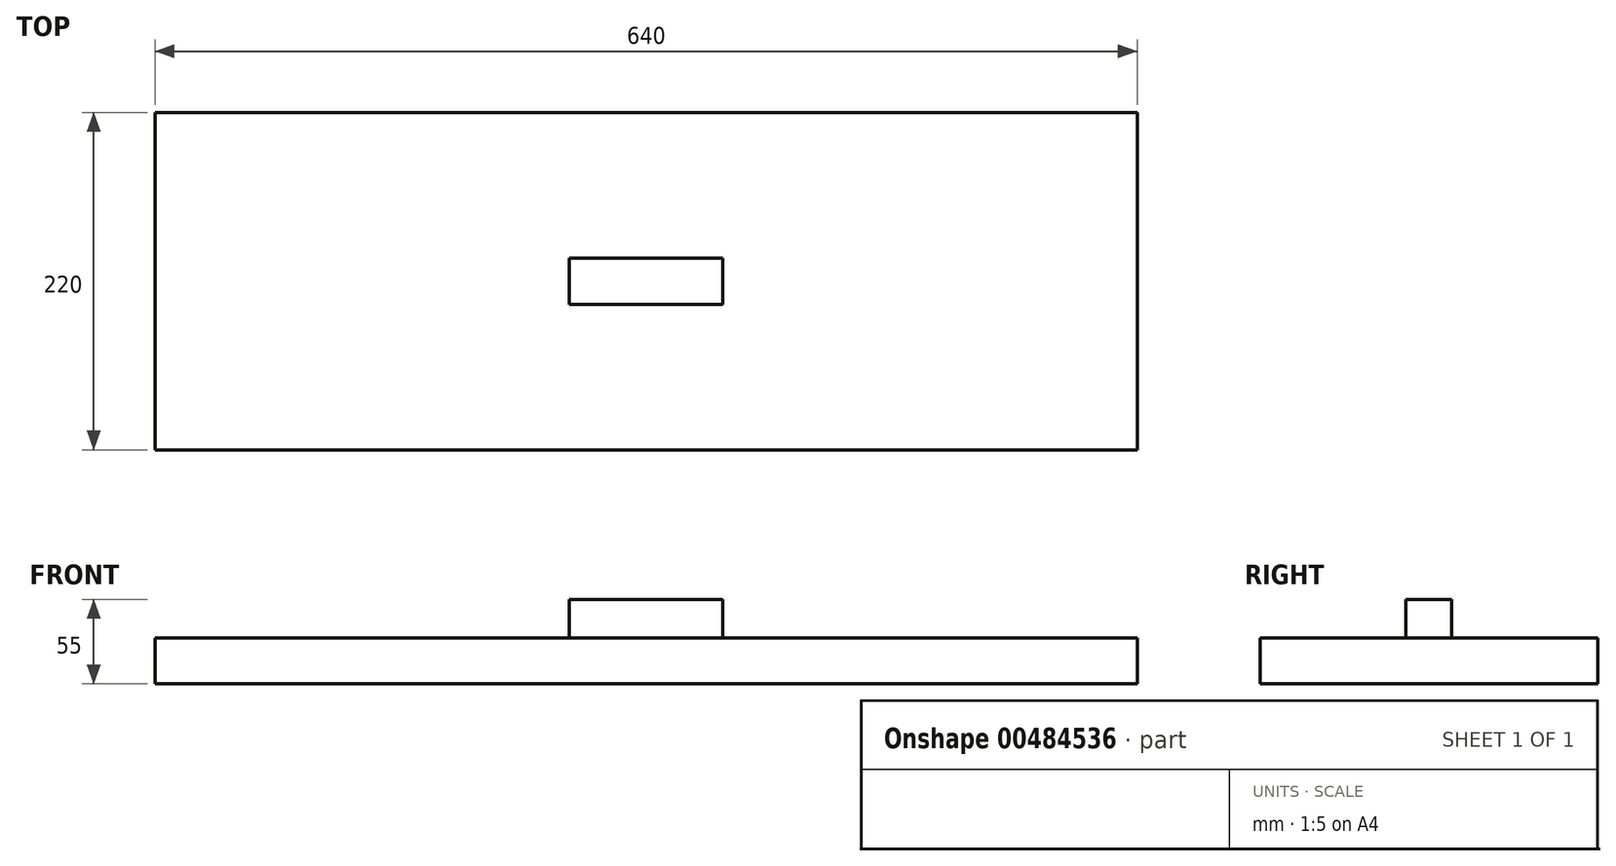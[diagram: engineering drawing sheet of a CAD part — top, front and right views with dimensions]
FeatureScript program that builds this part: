
annotation { "Feature Type Name" : "Feature", "Feature Type Description" : "" }
export const myFeature = defineFeature(function(context is Context, id is Id, definition is map)
    precondition{}
    {
        {
            var Q0;
            Q0=qCreatedBy(makeId("Top.planeOp"),FACE);
            var sketch = newSketch(context, id + "F0", { "sketchPlane" : qUnion([Q0])});
            skLineSegment(sketch, "E0.bottom", {"start": v(-509.87, -280.53) * mm, "end": v(130.13, -280.53) * mm});
            skLineSegment(sketch, "E0.top", {"start": v(-509.87, -60.53) * mm, "end": v(130.13, -60.53) * mm});
            skLineSegment(sketch, "E0.left", {"start": v(-509.87, -280.53) * mm, "end": v(-509.87, -60.53) * mm});
            skLineSegment(sketch, "E0.right", {"start": v(130.13, -280.53) * mm, "end": v(130.13, -60.53) * mm});
            skSolve(sketch);
        }
        {
            var Q0;
            Q0=qSketchRegion(id+"F0",true);
            extrude(context, id + "F1", {"entities" : qUnion([Q0]), "depth" : 30 * mm});
        }
        {
            var Q0;
            Q0=makeQuery(id+"F1.opExtrude","CAP_FACE",FACE,{"disambiguationData":[OSD([sQuery(id+"F0.wireOp",EDGE,"E0.bottom"),sQuery(id+"F0.wireOp",EDGE,"E0.top"),sQuery(id+"F0.wireOp",EDGE,"E0.left"),sQuery(id+"F0.wireOp",EDGE,"E0.right")])],"isStart":false});
            var sketch = newSketch(context, id + "F2", { "sketchPlane" : qUnion([Q0])});
            skLineSegment(sketch, "E1.bottom", {"start": v(-239.87, -185.53) * mm, "end": v(-139.87, -185.53) * mm});
            skLineSegment(sketch, "E1.top", {"start": v(-239.87, -155.53) * mm, "end": v(-139.87, -155.53) * mm});
            skLineSegment(sketch, "E1.left", {"start": v(-239.87, -185.53) * mm, "end": v(-239.87, -155.53) * mm});
            skLineSegment(sketch, "E1.right", {"start": v(-139.87, -185.53) * mm, "end": v(-139.87, -155.53) * mm});
            skSolve(sketch);
        }
        {
            var Q0;
            Q0=makeQuery(id+"F2.imprint","IMPRINT",FACE,{"disambiguationData":[TD([[makeQuery(id+"F2.imprint","IMPRINT",EDGE,{"derivedFrom":sQuery(id+"F2.wireOp",EDGE,"E1.bottom")}),1.0]])]});
            extrude(context, id + "F3", {"entities" : qUnion([Q0]), "operationType" : NewBodyOperationType.ADD, "depth" : 25 * mm});
        }
    });
